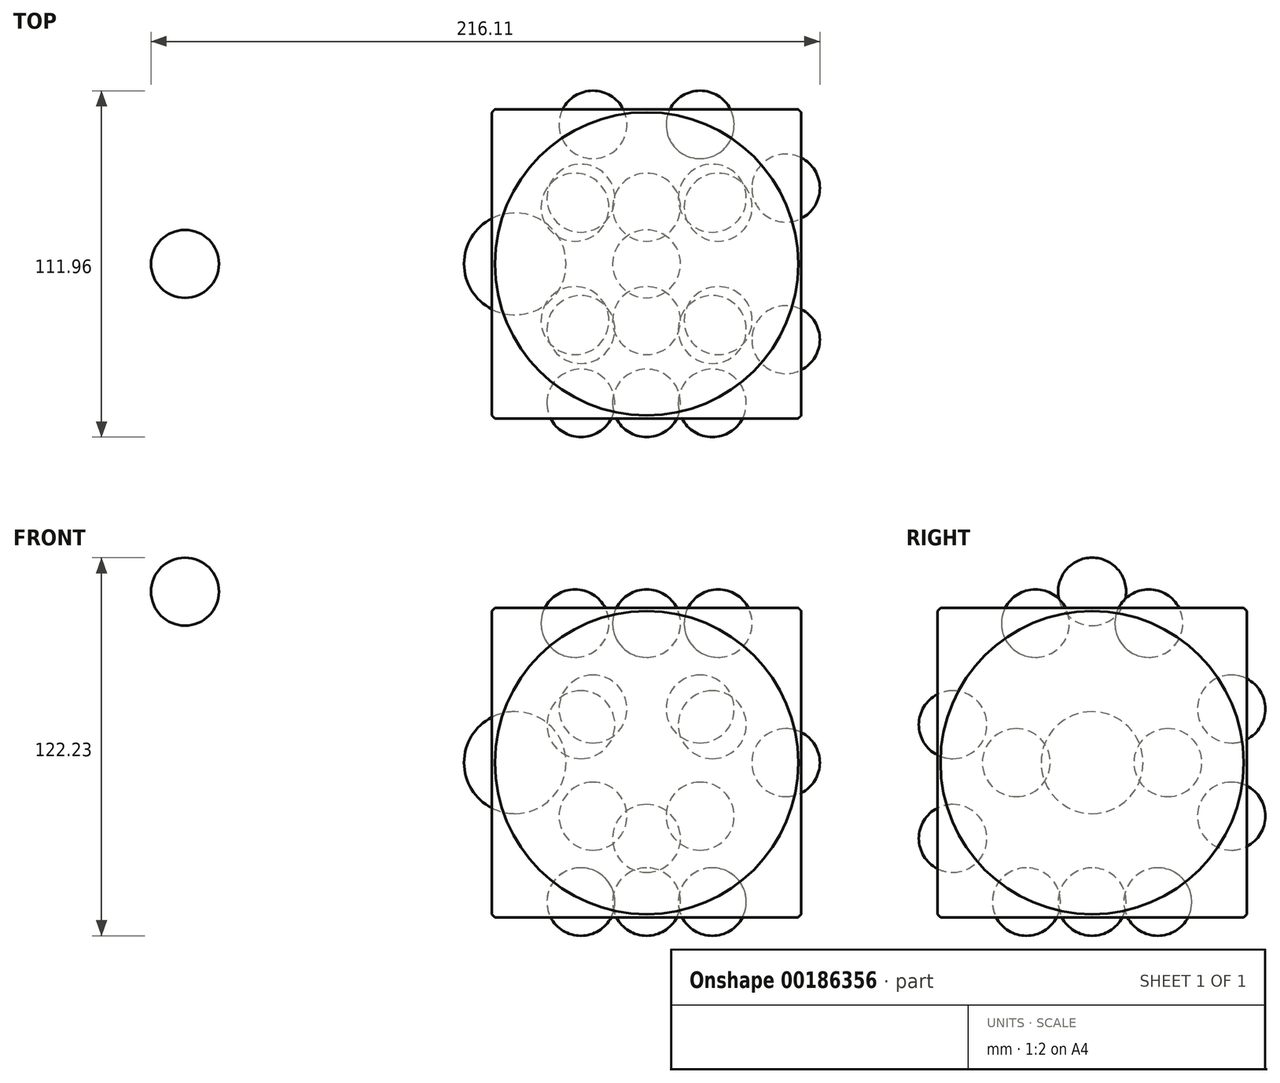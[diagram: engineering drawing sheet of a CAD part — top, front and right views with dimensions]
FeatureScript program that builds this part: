
annotation { "Feature Type Name" : "Feature", "Feature Type Description" : "" }
export const myFeature = defineFeature(function(context is Context, id is Id, definition is map)
    precondition{}
    {
        {
            var Q0;
            Q0=qCreatedBy(makeId("Front.planeOp"),FACE);
            var sketch = newSketch(context, id + "F0", { "sketchPlane" : qUnion([Q0])});
            skLineSegment(sketch, "E0.bottom", {"start": v(-50, 50) * mm, "end": v(50, 50) * mm});
            skLineSegment(sketch, "E0.top", {"start": v(-50, -50) * mm, "end": v(50, -50) * mm});
            skLineSegment(sketch, "E0.left", {"start": v(-50, 50) * mm, "end": v(-50, -50) * mm});
            skLineSegment(sketch, "E0.right", {"start": v(50, 50) * mm, "end": v(50, -50) * mm});
            skPoint(sketch, "E0.middle", {"position": v(0, 0) * mm});
            skSolve(sketch);
        }
        {
            var Q0;
            Q0=makeQuery(id+"F0.imprint","IMPRINT",FACE,{"disambiguationData":[TD([[makeQuery(id+"F0.imprint","IMPRINT",EDGE,{"derivedFrom":sQuery(id+"F0.wireOp",EDGE,"E0.bottom")}),-1.0]])]});
            extrude(context, id + "F1", {"entities" : qUnion([Q0]), "depth" : 50 * mm, "hasSecondDirection" : true, "secondDirectionOppositeDirection" : true, "secondDirectionDepth" : 50 * mm});
        }
        {
            var Q0;
            Q0=qCreatedBy(makeId("Front.planeOp"),FACE);
            var sketch = newSketch(context, id + "F2", { "sketchPlane" : qUnion([Q0])});
            skArc(sketch, "E1", {"start": v(143.18, 52.27) * mm, "mid": v(73.18, -17.73) * mm, "end": v(143.18, -87.73) * mm});
            skLineSegment(sketch, "E2", {"start": v(143.18, -17.73) * mm, "end": v(143.18, 52.27) * mm});
            skLineSegment(sketch, "E3", {"start": v(143.18, 52.27) * mm, "end": v(143.18, -87.73) * mm});
            skSolve(sketch);
        }
        {
            var Q0;
            {var subQ0=sQuery(id+"F2.wireOp",EDGE,"E1");Q0=makeQuery(id+"F2.imprint","IMPRINT",FACE,{"disambiguationData":[TD([[makeQuery(id+"F2.imprint","IMPRINT",EDGE,{"derivedFrom":subQ0}),1.0]])]});}
            var Q1;
            Q1=sQuery(id+"F2.wireOp",EDGE,"E3");
            revolve(context, id + "F3", {"entities" : qUnion([Q0]), "axis" : qUnion([Q1]), "revolveType" : RevolveType.FULL});
        }
        {
            var Q0;
            Q0=makeQuery(id+"F1.opExtrude","SWEPT_BODY",BODY,{"disambiguationData":[OSD([sQuery(id+"F0.wireOp",EDGE,"E0.bottom"),sQuery(id+"F0.wireOp",EDGE,"E0.top"),sQuery(id+"F0.wireOp",EDGE,"E0.left"),sQuery(id+"F0.wireOp",EDGE,"E0.right")])]});
            transform(context, id + "F4", {"entities" : qUnion([Q0]), "transformType" : TransformType.TRANSLATION_3D, "dx" : -200 * mm, "dy" : 0 * mm, "dz" : 0 * mm, "makeCopy" : true});
        }
        {
            var Q0;
            Q0=sQuery(id+"F2.wireOp",EDGE,"E3");
            cPoint(context, id + "F5", {"entities" : qUnion([Q0]), "parameter" : 0.5});
        }
        {
            var Q0;
            Q0=makeQuery(id+"F3.opRevolve","SWEPT_BODY",BODY,{"disambiguationData":[OSD([sQuery(id+"F2.wireOp",EDGE,"E1"),sQuery(id+"F2.wireOp",EDGE,"E3")])]});
            var Q1;
            Q1=qCreatedBy(makeId("Origin.pointOp"),VERTEX);
            var Q2;
            Q2 = qCreatedBy(id + "F5" ,VERTEX);
            transform(context, id + "F6", {"entities" : qUnion([Q0]), "transformType" : TransformType.TRANSLATION_ENTITY, "oppositeDirectionEntity" : true, "transformLine" : qUnion([Q1, Q2]), "makeCopy" : false});
        }
        {
            var Q0;
            Q0=makeQuery(id+"F3.opRevolve","SWEPT_BODY",BODY,{"disambiguationData":[OSD([sQuery(id+"F2.wireOp",EDGE,"E1"),sQuery(id+"F2.wireOp",EDGE,"E3")])]});
            var Q1;
            Q1=makeQuery(id+"F1.opExtrude","SWEPT_BODY",BODY,{"disambiguationData":[OSD([sQuery(id+"F0.wireOp",EDGE,"E0.bottom"),sQuery(id+"F0.wireOp",EDGE,"E0.top"),sQuery(id+"F0.wireOp",EDGE,"E0.left"),sQuery(id+"F0.wireOp",EDGE,"E0.right")])]});
            booleanBodies(context, id + "F7", {"operationType" : BooleanOperationType.SUBTRACTION, "tools" : qUnion([Q0]), "targets" : qUnion([Q1])});
        }
        {
            var Q0;
            Q0=makeQuery(id+"F1.opExtrude","SWEPT_BODY",BODY,{"disambiguationData":[OSD([sQuery(id+"F0.wireOp",EDGE,"E0.bottom"),sQuery(id+"F0.wireOp",EDGE,"E0.top"),sQuery(id+"F0.wireOp",EDGE,"E0.left"),sQuery(id+"F0.wireOp",EDGE,"E0.right")])]});
            transform(context, id + "F8", {"entities" : qUnion([Q0]), "transformType" : TransformType.TRANSLATION_3D, "dx" : -200 * mm, "dy" : 0 * mm, "dz" : 0 * mm, "makeCopy" : false});
        }
        {
            var Q0;
            Q0=makeQuery(id+"F1.opExtrude","SWEPT_BODY",BODY,{"disambiguationData":[OSD([sQuery(id+"F0.wireOp",EDGE,"E0.bottom"),sQuery(id+"F0.wireOp",EDGE,"E0.top"),sQuery(id+"F0.wireOp",EDGE,"E0.left"),sQuery(id+"F0.wireOp",EDGE,"E0.right")])]});
            var Q1;
            Q1=makeQuery(id+"F4.opPattern","COPY",BODY,{"derivedFrom":makeQuery(id+"F1.opExtrude","SWEPT_BODY",BODY,{"disambiguationData":[OSD([sQuery(id+"F0.wireOp",EDGE,"E0.bottom"),sQuery(id+"F0.wireOp",EDGE,"E0.top"),sQuery(id+"F0.wireOp",EDGE,"E0.left"),sQuery(id+"F0.wireOp",EDGE,"E0.right")])]}),"instanceName":"1"});
            booleanBodies(context, id + "F9", {"operationType" : BooleanOperationType.SUBTRACTION, "tools" : qUnion([Q0]), "targets" : qUnion([Q1])});
        }
        {
            var Q0;
            Q0=makeQuery(id+"F4.opPattern","COPY",BODY,{"derivedFrom":makeQuery(id+"F1.opExtrude","SWEPT_BODY",BODY,{"disambiguationData":[OSD([sQuery(id+"F0.wireOp",EDGE,"E0.bottom"),sQuery(id+"F0.wireOp",EDGE,"E0.top"),sQuery(id+"F0.wireOp",EDGE,"E0.left"),sQuery(id+"F0.wireOp",EDGE,"E0.right")])]}),"instanceName":"1"});
            transform(context, id + "F10", {"entities" : qUnion([Q0]), "transformType" : TransformType.TRANSLATION_3D, "dx" : 200 * mm, "dy" : 0 * mm, "dz" : 0 * mm, "makeCopy" : false});
        }
        {
            var Q0;
            Q0=qCreatedBy(makeId("Front.planeOp"),FACE);
            var sketch = newSketch(context, id + "F11", { "sketchPlane" : qUnion([Q0])});
            skArc(sketch, "E4", {"start": v(-149.15, 66.25) * mm, "mid": v(-160.13, 55.27) * mm, "end": v(-149.15, 44.28) * mm});
            skLineSegment(sketch, "E5", {"start": v(-149.15, 55.27) * mm, "end": v(-149.15, 66.25) * mm});
            skLineSegment(sketch, "E6", {"start": v(-149.15, 66.25) * mm, "end": v(-149.15, 44.28) * mm});
            skSolve(sketch);
        }
        {
            var Q0;
            {var subQ0=sQuery(id+"F11.wireOp",EDGE,"E4");Q0=makeQuery(id+"F11.imprint","IMPRINT",FACE,{"disambiguationData":[TD([[makeQuery(id+"F11.imprint","IMPRINT",EDGE,{"derivedFrom":subQ0}),1.0]])]});}
            var Q1;
            Q1=sQuery(id+"F11.wireOp",EDGE,"E5");
            revolve(context, id + "F12", {"entities" : qUnion([Q0]), "axis" : qUnion([Q1]), "revolveType" : RevolveType.FULL});
        }
        {
            var Q0;
            Q0=makeQuery(id+"F4.opPattern","COPY",FACE,{"derivedFrom":makeQuery(id+"F1.opExtrude","CAP_FACE",FACE,{"disambiguationData":[OSD([sQuery(id+"F0.wireOp",EDGE,"E0.bottom"),sQuery(id+"F0.wireOp",EDGE,"E0.top"),sQuery(id+"F0.wireOp",EDGE,"E0.left"),sQuery(id+"F0.wireOp",EDGE,"E0.right")])],"isStart":false}),"instanceName":"1"});
            var sketch = newSketch(context, id + "F13", { "sketchPlane" : qUnion([Q0])});
            skPoint(sketch, "E7", {"position": v(-21.21, 12.25) * mm});
            skPoint(sketch, "E8", {"position": v(21.21, 12.25) * mm});
            skPoint(sketch, "E9", {"position": v(0, -24.5) * mm});
            skPoint(sketch, "E10", {"position": v(0, 0) * mm});
            skLineSegment(sketch, "E11", {"start": v(0, 0) * mm, "end": v(-21.21, 12.25) * mm});
            skLineSegment(sketch, "E12", {"start": v(21.21, 12.25) * mm, "end": v(0, 0) * mm});
            skLineSegment(sketch, "E13", {"start": v(0, -24.5) * mm, "end": v(0, 0) * mm});
            skLineSegment(sketch, "E14", {"start": v(-21.21, 12.25) * mm, "end": v(-42.43, 24.5) * mm});
            skSolve(sketch);
        }
        {
            var Q0;
            Q0=makeQuery(id+"F12.opRevolve","SWEPT_BODY",BODY,{"disambiguationData":[OSD([sQuery(id+"F11.wireOp",EDGE,"E4"),sQuery(id+"F11.wireOp",EDGE,"E6")])]});
            var Q1;
            Q1=sQuery(id+"F11.wireOp",VERTEX,"E4.center");
            var Q2;
            Q2=sQuery(id+"F13.wireOp",VERTEX,"E7");
            transform(context, id + "F14", {"entities" : qUnion([Q0]), "transformType" : TransformType.TRANSLATION_ENTITY, "oppositeDirectionEntity" : false, "transformLine" : qUnion([Q1, Q2]), "makeCopy" : true});
        }
        {
            var Q0;
            Q0=sQuery(id+"F11.wireOp",EDGE,"E6");
            cPoint(context, id + "F15", {"entities" : qUnion([Q0]), "parameter" : 0.5});
        }
        {
            var Q0;
            Q0=makeQuery(id+"F12.opRevolve","SWEPT_BODY",BODY,{"disambiguationData":[OSD([sQuery(id+"F11.wireOp",EDGE,"E4"),sQuery(id+"F11.wireOp",EDGE,"E6")])]});
            var Q1;
            Q1 = qCreatedBy(id + "F15" ,VERTEX);
            var Q2;
            Q2=sQuery(id+"F13.wireOp",VERTEX,"E8");
            transform(context, id + "F16", {"entities" : qUnion([Q0]), "transformType" : TransformType.TRANSLATION_ENTITY, "oppositeDirectionEntity" : false, "transformLine" : qUnion([Q1, Q2]), "makeCopy" : true});
        }
        {
            var Q0;
            Q0=makeQuery(id+"F12.opRevolve","SWEPT_BODY",BODY,{"disambiguationData":[OSD([sQuery(id+"F11.wireOp",EDGE,"E4"),sQuery(id+"F11.wireOp",EDGE,"E6")])]});
            var Q1;
            Q1=sQuery(id+"F11.wireOp",VERTEX,"E4.center");
            var Q2;
            Q2=sQuery(id+"F13.wireOp",VERTEX,"E9");
            transform(context, id + "F17", {"entities" : qUnion([Q0]), "transformType" : TransformType.TRANSLATION_ENTITY, "oppositeDirectionEntity" : false, "transformLine" : qUnion([Q1, Q2]), "makeCopy" : true});
        }
        {
            var Q0;
            Q0=makeQuery(id+"F4.opPattern","COPY",FACE,{"derivedFrom":makeQuery(id+"F1.opExtrude","SWEPT_FACE",FACE,{"disambiguationData":[OSD([sQuery(id+"F0.wireOp",EDGE,"E0.right")])]}),"instanceName":"1"});
            var sketch = newSketch(context, id + "F18", { "sketchPlane" : qUnion([Q0])});
            skLineSegment(sketch, "E15", {"start": v(0, 0) * mm, "end": v(-24.5, 0) * mm});
            skLineSegment(sketch, "E16", {"start": v(-24.5, 0) * mm, "end": v(-48.99, 0) * mm});
            skLineSegment(sketch, "E17", {"start": v(0, 0) * mm, "end": v(24.5, 0) * mm});
            skSolve(sketch);
        }
        {
            var Q0;
            Q0=makeQuery(id+"F12.opRevolve","SWEPT_BODY",BODY,{"disambiguationData":[OSD([sQuery(id+"F11.wireOp",EDGE,"E4"),sQuery(id+"F11.wireOp",EDGE,"E6")])]});
            var Q1;
            Q1=sQuery(id+"F11.wireOp",VERTEX,"E4.center");
            var Q2;
            Q2=sQuery(id+"F18.wireOp",VERTEX,"E16.start");
            transform(context, id + "F19", {"entities" : qUnion([Q0]), "transformType" : TransformType.TRANSLATION_ENTITY, "oppositeDirectionEntity" : false, "transformLine" : qUnion([Q1, Q2]), "makeCopy" : true});
        }
        {
            var Q0;
            Q0=sQuery(id+"F11.wireOp",EDGE,"E6");
            cPoint(context, id + "F20", {"entities" : qUnion([Q0]), "parameter" : 0.5});
        }
        {
            var Q0;
            Q0=makeQuery(id+"F12.opRevolve","SWEPT_BODY",BODY,{"disambiguationData":[OSD([sQuery(id+"F11.wireOp",EDGE,"E4"),sQuery(id+"F11.wireOp",EDGE,"E6")])]});
            var Q1;
            Q1 = qCreatedBy(id + "F20" ,VERTEX);
            var Q2;
            Q2=sQuery(id+"F18.wireOp",VERTEX,"E17.end");
            transform(context, id + "F21", {"entities" : qUnion([Q0]), "transformType" : TransformType.TRANSLATION_ENTITY, "oppositeDirectionEntity" : false, "transformLine" : qUnion([Q1, Q2]), "makeCopy" : true});
        }
        {
            var Q0;
            Q0=makeQuery(id+"F4.opPattern","COPY",FACE,{"derivedFrom":makeQuery(id+"F1.opExtrude","CAP_FACE",FACE,{"disambiguationData":[OSD([sQuery(id+"F0.wireOp",EDGE,"E0.bottom"),sQuery(id+"F0.wireOp",EDGE,"E0.top"),sQuery(id+"F0.wireOp",EDGE,"E0.left"),sQuery(id+"F0.wireOp",EDGE,"E0.right")])],"isStart":true}),"instanceName":"1"});
            var sketch = newSketch(context, id + "F22", { "sketchPlane" : qUnion([Q0])});
            skLineSegment(sketch, "E18", {"start": v(0, 0) * mm, "end": v(-17.32, 17.32) * mm});
            skLineSegment(sketch, "E19", {"start": v(-17.32, 17.32) * mm, "end": v(-34.64, 34.64) * mm});
            skLineSegment(sketch, "E20", {"start": v(0, 0) * mm, "end": v(17.32, 17.32) * mm});
            skLineSegment(sketch, "E21", {"start": v(0, 0) * mm, "end": v(-17.32, -17.32) * mm});
            skLineSegment(sketch, "E22", {"start": v(0, 0) * mm, "end": v(17.32, -17.32) * mm});
            skSolve(sketch);
        }
        {
            var Q0;
            Q0=makeQuery(id+"F12.opRevolve","SWEPT_BODY",BODY,{"disambiguationData":[OSD([sQuery(id+"F11.wireOp",EDGE,"E4"),sQuery(id+"F11.wireOp",EDGE,"E6")])]});
            var Q1;
            Q1=sQuery(id+"F11.wireOp",VERTEX,"E4.center");
            var Q2;
            Q2=sQuery(id+"F22.wireOp",VERTEX,"E20.end");
            transform(context, id + "F23", {"entities" : qUnion([Q0]), "transformType" : TransformType.TRANSLATION_ENTITY, "oppositeDirectionEntity" : false, "transformLine" : qUnion([Q1, Q2]), "makeCopy" : true});
        }
        {
            var Q0;
            Q0=sQuery(id+"F11.wireOp",EDGE,"E6");
            cPoint(context, id + "F24", {"entities" : qUnion([Q0]), "parameter" : 0.5});
        }
        {
            var Q0;
            Q0=makeQuery(id+"F12.opRevolve","SWEPT_BODY",BODY,{"disambiguationData":[OSD([sQuery(id+"F11.wireOp",EDGE,"E4"),sQuery(id+"F11.wireOp",EDGE,"E6")])]});
            var Q1;
            Q1=sQuery(id+"F22.wireOp",VERTEX,"E22.end");
            var Q2;
            Q2 = qCreatedBy(id + "F24" ,VERTEX);
            transform(context, id + "F25", {"entities" : qUnion([Q0]), "transformType" : TransformType.TRANSLATION_ENTITY, "oppositeDirectionEntity" : true, "transformLine" : qUnion([Q1, Q2]), "makeCopy" : true});
        }
        {
            var Q0;
            Q0=makeQuery(id+"F12.opRevolve","SWEPT_BODY",BODY,{"disambiguationData":[OSD([sQuery(id+"F11.wireOp",EDGE,"E4"),sQuery(id+"F11.wireOp",EDGE,"E6")])]});
            var Q1;
            Q1=sQuery(id+"F11.wireOp",VERTEX,"E4.center");
            var Q2;
            Q2=sQuery(id+"F22.wireOp",VERTEX,"E21.end");
            transform(context, id + "F26", {"entities" : qUnion([Q0]), "transformType" : TransformType.TRANSLATION_ENTITY, "oppositeDirectionEntity" : false, "transformLine" : qUnion([Q1, Q2]), "makeCopy" : true});
        }
        {
            var Q0;
            Q0=makeQuery(id+"F12.opRevolve","SWEPT_BODY",BODY,{"disambiguationData":[OSD([sQuery(id+"F11.wireOp",EDGE,"E4"),sQuery(id+"F11.wireOp",EDGE,"E6")])]});
            var Q1;
            Q1=sQuery(id+"F11.wireOp",VERTEX,"E4.center");
            var Q2;
            Q2=sQuery(id+"F22.wireOp",VERTEX,"E19.start");
            transform(context, id + "F27", {"entities" : qUnion([Q0]), "transformType" : TransformType.TRANSLATION_ENTITY, "oppositeDirectionEntity" : false, "transformLine" : qUnion([Q1, Q2]), "makeCopy" : true});
        }
        {
            var Q0;
            Q0=makeQuery(id+"F4.opPattern","COPY",FACE,{"derivedFrom":makeQuery(id+"F1.opExtrude","SWEPT_FACE",FACE,{"disambiguationData":[OSD([sQuery(id+"F0.wireOp",EDGE,"E0.bottom")])]}),"instanceName":"1"});
            var sketch = newSketch(context, id + "F28", { "sketchPlane" : qUnion([Q0])});
            skLineSegment(sketch, "E23", {"start": v(0, 0) * mm, "end": v(0, -18.32) * mm});
            skLineSegment(sketch, "E24", {"start": v(0, 0) * mm, "end": v(0, 18.32) * mm});
            skLineSegment(sketch, "E25", {"start": v(0, 18.32) * mm, "end": v(23.13, 18.32) * mm});
            skLineSegment(sketch, "E26", {"start": v(0, 18.32) * mm, "end": v(-23.13, 18.32) * mm});
            skLineSegment(sketch, "E27", {"start": v(0, -18.32) * mm, "end": v(-23.13, -18.32) * mm});
            skLineSegment(sketch, "E28", {"start": v(0, -18.32) * mm, "end": v(23.13, -18.32) * mm});
            skSolve(sketch);
        }
        {
            var Q0;
            Q0=makeQuery(id+"F12.opRevolve","SWEPT_BODY",BODY,{"disambiguationData":[OSD([sQuery(id+"F11.wireOp",EDGE,"E4"),sQuery(id+"F11.wireOp",EDGE,"E6")])]});
            var Q1;
            Q1=sQuery(id+"F11.wireOp",VERTEX,"E4.center");
            var Q2;
            Q2=sQuery(id+"F28.wireOp",VERTEX,"E27.end");
            transform(context, id + "F29", {"entities" : qUnion([Q0]), "transformType" : TransformType.TRANSLATION_ENTITY, "oppositeDirectionEntity" : false, "transformLine" : qUnion([Q1, Q2]), "makeCopy" : true});
        }
        {
            var Q0;
            Q0=makeQuery(id+"F12.opRevolve","SWEPT_BODY",BODY,{"disambiguationData":[OSD([sQuery(id+"F11.wireOp",EDGE,"E4"),sQuery(id+"F11.wireOp",EDGE,"E6")])]});
            var Q1;
            Q1=sQuery(id+"F11.wireOp",VERTEX,"E4.center");
            var Q2;
            Q2=sQuery(id+"F28.wireOp",VERTEX,"E28.start");
            transform(context, id + "F30", {"entities" : qUnion([Q0]), "transformType" : TransformType.TRANSLATION_ENTITY, "oppositeDirectionEntity" : false, "transformLine" : qUnion([Q1, Q2]), "makeCopy" : true});
        }
        {
            var Q0;
            Q0=makeQuery(id+"F12.opRevolve","SWEPT_BODY",BODY,{"disambiguationData":[OSD([sQuery(id+"F11.wireOp",EDGE,"E4"),sQuery(id+"F11.wireOp",EDGE,"E6")])]});
            var Q1;
            Q1=sQuery(id+"F11.wireOp",VERTEX,"E4.center");
            var Q2;
            Q2=sQuery(id+"F28.wireOp",VERTEX,"E28.end");
            transform(context, id + "F31", {"entities" : qUnion([Q0]), "transformType" : TransformType.TRANSLATION_ENTITY, "oppositeDirectionEntity" : false, "transformLine" : qUnion([Q1, Q2]), "makeCopy" : true});
        }
        {
            var Q0;
            Q0=makeQuery(id+"F12.opRevolve","SWEPT_BODY",BODY,{"disambiguationData":[OSD([sQuery(id+"F11.wireOp",EDGE,"E4"),sQuery(id+"F11.wireOp",EDGE,"E6")])]});
            var Q1;
            Q1=sQuery(id+"F11.wireOp",VERTEX,"E4.center");
            var Q2;
            Q2=sQuery(id+"F28.wireOp",VERTEX,"E26.start");
            transform(context, id + "F32", {"entities" : qUnion([Q0]), "transformType" : TransformType.TRANSLATION_ENTITY, "oppositeDirectionEntity" : false, "transformLine" : qUnion([Q1, Q2]), "makeCopy" : true});
        }
        {
            var Q0;
            Q0=makeQuery(id+"F12.opRevolve","SWEPT_BODY",BODY,{"disambiguationData":[OSD([sQuery(id+"F11.wireOp",EDGE,"E4"),sQuery(id+"F11.wireOp",EDGE,"E6")])]});
            var Q1;
            Q1=sQuery(id+"F11.wireOp",VERTEX,"E4.center");
            var Q2;
            Q2=sQuery(id+"F28.wireOp",VERTEX,"E26.end");
            transform(context, id + "F33", {"entities" : qUnion([Q0]), "transformType" : TransformType.TRANSLATION_ENTITY, "oppositeDirectionEntity" : false, "transformLine" : qUnion([Q1, Q2]), "makeCopy" : true});
        }
        {
            var Q0;
            Q0=makeQuery(id+"F12.opRevolve","SWEPT_BODY",BODY,{"disambiguationData":[OSD([sQuery(id+"F11.wireOp",EDGE,"E4"),sQuery(id+"F11.wireOp",EDGE,"E6")])]});
            var Q1;
            Q1=sQuery(id+"F11.wireOp",VERTEX,"E4.center");
            var Q2;
            Q2=sQuery(id+"F28.wireOp",VERTEX,"E25.end");
            transform(context, id + "F34", {"entities" : qUnion([Q0]), "transformType" : TransformType.TRANSLATION_ENTITY, "oppositeDirectionEntity" : false, "transformLine" : qUnion([Q1, Q2]), "makeCopy" : true});
        }
        {
            var Q0;
            Q0=makeQuery(id+"F4.opPattern","COPY",FACE,{"derivedFrom":makeQuery(id+"F1.opExtrude","SWEPT_FACE",FACE,{"disambiguationData":[OSD([sQuery(id+"F0.wireOp",EDGE,"E0.left")])]}),"instanceName":"1"});
            var sketch = newSketch(context, id + "F35", { "sketchPlane" : qUnion([Q0])});
            skPoint(sketch, "E29", {"position": v(0, 0) * mm});
            skSolve(sketch);
        }
        {
            var Q0;
            Q0=sQuery(id+"F11.wireOp",EDGE,"E6");
            cPoint(context, id + "F36", {"entities" : qUnion([Q0]), "parameter" : 0.5});
        }
        {
            var Q0;
            Q0=makeQuery(id+"F12.opRevolve","SWEPT_BODY",BODY,{"disambiguationData":[OSD([sQuery(id+"F11.wireOp",EDGE,"E4"),sQuery(id+"F11.wireOp",EDGE,"E6")])]});
            var Q1;
            Q1 = qCreatedBy(id + "F36" ,VERTEX);
            var Q2;
            Q2=sQuery(id+"F35.wireOp",VERTEX,"E29");
            transform(context, id + "F37", {"entities" : qUnion([Q0]), "transformType" : TransformType.TRANSLATION_ENTITY, "oppositeDirectionEntity" : false, "transformLine" : qUnion([Q1, Q2]), "makeCopy" : true});
        }
        {
            var Q0;
            Q0=makeQuery(id+"F4.opPattern","COPY",FACE,{"derivedFrom":makeQuery(id+"F1.opExtrude","SWEPT_FACE",FACE,{"disambiguationData":[OSD([sQuery(id+"F0.wireOp",EDGE,"E0.top")])]}),"instanceName":"1"});
            var sketch = newSketch(context, id + "F38", { "sketchPlane" : qUnion([Q0])});
            skLineSegment(sketch, "E30", {"start": v(0, 0) * mm, "end": v(-21.23, -21.23) * mm});
            skLineSegment(sketch, "E31", {"start": v(0, 0) * mm, "end": v(-21.23, 21.23) * mm});
            skLineSegment(sketch, "E32", {"start": v(0, 0) * mm, "end": v(21.23, -21.23) * mm});
            skLineSegment(sketch, "E33", {"start": v(0, 0) * mm, "end": v(21.23, 21.23) * mm});
            skSolve(sketch);
        }
        {
            var Q0;
            Q0=makeQuery(id+"F12.opRevolve","SWEPT_BODY",BODY,{"disambiguationData":[OSD([sQuery(id+"F11.wireOp",EDGE,"E4"),sQuery(id+"F11.wireOp",EDGE,"E6")])]});
            var Q1;
            Q1=sQuery(id+"F11.wireOp",VERTEX,"E4.center");
            var Q2;
            Q2=sQuery(id+"F38.wireOp",VERTEX,"E33.start");
            transform(context, id + "F39", {"entities" : qUnion([Q0]), "transformType" : TransformType.TRANSLATION_ENTITY, "oppositeDirectionEntity" : false, "transformLine" : qUnion([Q1, Q2]), "makeCopy" : true});
        }
        {
            var Q0;
            Q0=sQuery(id+"F11.wireOp",EDGE,"E6");
            cPoint(context, id + "F40", {"entities" : qUnion([Q0]), "parameter" : 0.5});
        }
        {
            var Q0;
            Q0=makeQuery(id+"F12.opRevolve","SWEPT_BODY",BODY,{"disambiguationData":[OSD([sQuery(id+"F11.wireOp",EDGE,"E4"),sQuery(id+"F11.wireOp",EDGE,"E6")])]});
            var Q1;
            Q1=sQuery(id+"F38.wireOp",VERTEX,"E31.end");
            var Q2;
            Q2 = qCreatedBy(id + "F40" ,VERTEX);
            transform(context, id + "F41", {"entities" : qUnion([Q0]), "transformType" : TransformType.TRANSLATION_ENTITY, "oppositeDirectionEntity" : true, "transformLine" : qUnion([Q1, Q2]), "makeCopy" : true});
        }
        {
            var Q0;
            Q0=makeQuery(id+"F12.opRevolve","SWEPT_BODY",BODY,{"disambiguationData":[OSD([sQuery(id+"F11.wireOp",EDGE,"E4"),sQuery(id+"F11.wireOp",EDGE,"E6")])]});
            var Q1;
            Q1=sQuery(id+"F11.wireOp",VERTEX,"E4.center");
            var Q2;
            Q2=sQuery(id+"F38.wireOp",VERTEX,"E30.end");
            transform(context, id + "F42", {"entities" : qUnion([Q0]), "transformType" : TransformType.TRANSLATION_ENTITY, "oppositeDirectionEntity" : false, "transformLine" : qUnion([Q1, Q2]), "makeCopy" : true});
        }
        {
            var Q0;
            Q0=makeQuery(id+"F12.opRevolve","SWEPT_BODY",BODY,{"disambiguationData":[OSD([sQuery(id+"F11.wireOp",EDGE,"E4"),sQuery(id+"F11.wireOp",EDGE,"E6")])]});
            var Q1;
            Q1=sQuery(id+"F38.wireOp",VERTEX,"E32.end");
            var Q2;
            Q2=sQuery(id+"F11.wireOp",VERTEX,"E4.center");
            transform(context, id + "F43", {"entities" : qUnion([Q0]), "transformType" : TransformType.TRANSLATION_ENTITY, "oppositeDirectionEntity" : true, "transformLine" : qUnion([Q1, Q2]), "makeCopy" : true});
        }
        {
            var Q0;
            Q0=makeQuery(id+"F12.opRevolve","SWEPT_BODY",BODY,{"disambiguationData":[OSD([sQuery(id+"F11.wireOp",EDGE,"E4"),sQuery(id+"F11.wireOp",EDGE,"E6")])]});
            var Q1;
            Q1=sQuery(id+"F38.wireOp",VERTEX,"E33.end");
            var Q2;
            Q2=sQuery(id+"F11.wireOp",VERTEX,"E4.center");
            transform(context, id + "F44", {"entities" : qUnion([Q0]), "transformType" : TransformType.TRANSLATION_ENTITY, "oppositeDirectionEntity" : true, "transformLine" : qUnion([Q1, Q2]), "makeCopy" : true});
        }
        {
            var Q0;
            Q0=makeQuery(id+"F25.opPattern","COPY",BODY,{"derivedFrom":makeQuery(id+"F12.opRevolve","SWEPT_BODY",BODY,{"disambiguationData":[OSD([sQuery(id+"F11.wireOp",EDGE,"E4"),sQuery(id+"F11.wireOp",EDGE,"E6")])]}),"instanceName":"1"});
            var Q1;
            Q1=makeQuery(id+"F23.opPattern","COPY",BODY,{"derivedFrom":makeQuery(id+"F12.opRevolve","SWEPT_BODY",BODY,{"disambiguationData":[OSD([sQuery(id+"F11.wireOp",EDGE,"E4"),sQuery(id+"F11.wireOp",EDGE,"E6")])]}),"instanceName":"1"});
            var Q2;
            Q2=makeQuery(id+"F27.opPattern","COPY",BODY,{"derivedFrom":makeQuery(id+"F12.opRevolve","SWEPT_BODY",BODY,{"disambiguationData":[OSD([sQuery(id+"F11.wireOp",EDGE,"E4"),sQuery(id+"F11.wireOp",EDGE,"E6")])]}),"instanceName":"1"});
            var Q3;
            Q3=makeQuery(id+"F26.opPattern","COPY",BODY,{"derivedFrom":makeQuery(id+"F12.opRevolve","SWEPT_BODY",BODY,{"disambiguationData":[OSD([sQuery(id+"F11.wireOp",EDGE,"E4"),sQuery(id+"F11.wireOp",EDGE,"E6")])]}),"instanceName":"1"});
            transform(context, id + "F45", {"entities" : qUnion([Q0, Q1, Q2, Q3]), "transformType" : TransformType.TRANSLATION_3D, "dx" : 0 * mm, "dy" : -5 * mm, "dz" : 0 * mm, "makeCopy" : false});
        }
        {
            var Q0;
            Q0=makeQuery(id+"F29.opPattern","COPY",BODY,{"derivedFrom":makeQuery(id+"F12.opRevolve","SWEPT_BODY",BODY,{"disambiguationData":[OSD([sQuery(id+"F11.wireOp",EDGE,"E4"),sQuery(id+"F11.wireOp",EDGE,"E6")])]}),"instanceName":"1"});
            var Q1;
            Q1=makeQuery(id+"F30.opPattern","COPY",BODY,{"derivedFrom":makeQuery(id+"F12.opRevolve","SWEPT_BODY",BODY,{"disambiguationData":[OSD([sQuery(id+"F11.wireOp",EDGE,"E4"),sQuery(id+"F11.wireOp",EDGE,"E6")])]}),"instanceName":"1"});
            var Q2;
            Q2=makeQuery(id+"F31.opPattern","COPY",BODY,{"derivedFrom":makeQuery(id+"F12.opRevolve","SWEPT_BODY",BODY,{"disambiguationData":[OSD([sQuery(id+"F11.wireOp",EDGE,"E4"),sQuery(id+"F11.wireOp",EDGE,"E6")])]}),"instanceName":"1"});
            var Q3;
            Q3=makeQuery(id+"F34.opPattern","COPY",BODY,{"derivedFrom":makeQuery(id+"F12.opRevolve","SWEPT_BODY",BODY,{"disambiguationData":[OSD([sQuery(id+"F11.wireOp",EDGE,"E4"),sQuery(id+"F11.wireOp",EDGE,"E6")])]}),"instanceName":"1"});
            var Q4;
            Q4=makeQuery(id+"F32.opPattern","COPY",BODY,{"derivedFrom":makeQuery(id+"F12.opRevolve","SWEPT_BODY",BODY,{"disambiguationData":[OSD([sQuery(id+"F11.wireOp",EDGE,"E4"),sQuery(id+"F11.wireOp",EDGE,"E6")])]}),"instanceName":"1"});
            var Q5;
            Q5=makeQuery(id+"F33.opPattern","COPY",BODY,{"derivedFrom":makeQuery(id+"F12.opRevolve","SWEPT_BODY",BODY,{"disambiguationData":[OSD([sQuery(id+"F11.wireOp",EDGE,"E4"),sQuery(id+"F11.wireOp",EDGE,"E6")])]}),"instanceName":"1"});
            transform(context, id + "F46", {"entities" : qUnion([Q0, Q1, Q2, Q3, Q4, Q5]), "transformType" : TransformType.TRANSLATION_3D, "dx" : 0 * mm, "dy" : 0 * mm, "dz" : -5 * mm, "makeCopy" : false});
        }
        {
            var Q0;
            Q0=makeQuery(id+"F39.opPattern","COPY",BODY,{"derivedFrom":makeQuery(id+"F12.opRevolve","SWEPT_BODY",BODY,{"disambiguationData":[OSD([sQuery(id+"F11.wireOp",EDGE,"E4"),sQuery(id+"F11.wireOp",EDGE,"E6")])]}),"instanceName":"1"});
            var Q1;
            Q1=makeQuery(id+"F44.opPattern","COPY",BODY,{"derivedFrom":makeQuery(id+"F12.opRevolve","SWEPT_BODY",BODY,{"disambiguationData":[OSD([sQuery(id+"F11.wireOp",EDGE,"E4"),sQuery(id+"F11.wireOp",EDGE,"E6")])]}),"instanceName":"1"});
            var Q2;
            Q2=makeQuery(id+"F43.opPattern","COPY",BODY,{"derivedFrom":makeQuery(id+"F12.opRevolve","SWEPT_BODY",BODY,{"disambiguationData":[OSD([sQuery(id+"F11.wireOp",EDGE,"E4"),sQuery(id+"F11.wireOp",EDGE,"E6")])]}),"instanceName":"1"});
            var Q3;
            Q3=makeQuery(id+"F41.opPattern","COPY",BODY,{"derivedFrom":makeQuery(id+"F12.opRevolve","SWEPT_BODY",BODY,{"disambiguationData":[OSD([sQuery(id+"F11.wireOp",EDGE,"E4"),sQuery(id+"F11.wireOp",EDGE,"E6")])]}),"instanceName":"1"});
            var Q4;
            Q4=makeQuery(id+"F42.opPattern","COPY",BODY,{"derivedFrom":makeQuery(id+"F12.opRevolve","SWEPT_BODY",BODY,{"disambiguationData":[OSD([sQuery(id+"F11.wireOp",EDGE,"E4"),sQuery(id+"F11.wireOp",EDGE,"E6")])]}),"instanceName":"1"});
            transform(context, id + "F47", {"entities" : qUnion([Q0, Q1, Q2, Q3, Q4]), "transformType" : TransformType.TRANSLATION_3D, "dx" : 0 * mm, "dy" : 0 * mm, "dz" : 5 * mm, "makeCopy" : false});
        }
        {
            var Q0;
            Q0=makeQuery(id+"F17.opPattern","COPY",BODY,{"derivedFrom":makeQuery(id+"F12.opRevolve","SWEPT_BODY",BODY,{"disambiguationData":[OSD([sQuery(id+"F11.wireOp",EDGE,"E4"),sQuery(id+"F11.wireOp",EDGE,"E6")])]}),"instanceName":"1"});
            var Q1;
            Q1=makeQuery(id+"F14.opPattern","COPY",BODY,{"derivedFrom":makeQuery(id+"F12.opRevolve","SWEPT_BODY",BODY,{"disambiguationData":[OSD([sQuery(id+"F11.wireOp",EDGE,"E4"),sQuery(id+"F11.wireOp",EDGE,"E6")])]}),"instanceName":"1"});
            var Q2;
            Q2=makeQuery(id+"F16.opPattern","COPY",BODY,{"derivedFrom":makeQuery(id+"F12.opRevolve","SWEPT_BODY",BODY,{"disambiguationData":[OSD([sQuery(id+"F11.wireOp",EDGE,"E4"),sQuery(id+"F11.wireOp",EDGE,"E6")])]}),"instanceName":"1"});
            transform(context, id + "F48", {"entities" : qUnion([Q0, Q1, Q2]), "transformType" : TransformType.TRANSLATION_3D, "dx" : 0 * mm, "dy" : 5 * mm, "dz" : 0 * mm, "makeCopy" : false});
        }
        {
            var Q0;
            Q0=makeQuery(id+"F19.opPattern","COPY",BODY,{"derivedFrom":makeQuery(id+"F12.opRevolve","SWEPT_BODY",BODY,{"disambiguationData":[OSD([sQuery(id+"F11.wireOp",EDGE,"E4"),sQuery(id+"F11.wireOp",EDGE,"E6")])]}),"instanceName":"1"});
            var Q1;
            Q1=makeQuery(id+"F21.opPattern","COPY",BODY,{"derivedFrom":makeQuery(id+"F12.opRevolve","SWEPT_BODY",BODY,{"disambiguationData":[OSD([sQuery(id+"F11.wireOp",EDGE,"E4"),sQuery(id+"F11.wireOp",EDGE,"E6")])]}),"instanceName":"1"});
            transform(context, id + "F49", {"entities" : qUnion([Q0, Q1]), "transformType" : TransformType.TRANSLATION_3D, "dx" : -5 * mm, "dy" : 0 * mm, "dz" : 0 * mm, "makeCopy" : false});
        }
        {
            var Q0;
            Q0=makeQuery(id+"F37.opPattern","COPY",BODY,{"derivedFrom":makeQuery(id+"F12.opRevolve","SWEPT_BODY",BODY,{"disambiguationData":[OSD([sQuery(id+"F11.wireOp",EDGE,"E4"),sQuery(id+"F11.wireOp",EDGE,"E6")])]}),"instanceName":"1"});
            var Q1;
            Q1=sQuery(id+"F35.wireOp",VERTEX,"E29");
            transform(context, id + "F50", {"entities" : qUnion([Q0]), "transformType" : TransformType.TRANSLATION_3D, "dx" : 5 * mm, "dy" : 0 * mm, "dz" : 0 * mm, "makeCopy" : false});
        }
        {
            var Q0;
            Q0=makeQuery(id+"F37.opPattern","COPY",BODY,{"derivedFrom":makeQuery(id+"F12.opRevolve","SWEPT_BODY",BODY,{"disambiguationData":[OSD([sQuery(id+"F11.wireOp",EDGE,"E4"),sQuery(id+"F11.wireOp",EDGE,"E6")])]}),"instanceName":"1"});
            var Q1;
            Q1=sQuery(id+"F35.wireOp",VERTEX,"E29");
            transform(context, id + "F51", {"entities" : qUnion([Q0]), "transformType" : TransformType.SCALE_UNIFORMLY, "scale" : 1.5, "scalePoint" : qUnion([Q1]), "makeCopy" : false});
        }
    });
